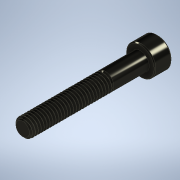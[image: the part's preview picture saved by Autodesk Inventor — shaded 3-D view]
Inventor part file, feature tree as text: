
AUTODESK INVENTOR PART (.ipt)
format: ipt  version: 2020 (Build 240168000, 168)  size: 840,704 bytes
history: native  units: in
note: dims shown in document units (in); Inventor stores cm internally (conversion verified against a paired STEP export)
features: chamfer x1
ambient origin geometry x8: Origin, YZ Plane, XZ Plane, XY Plane, X Axis, Y Axis, Z Axis, Center Point
bodies: Solid1 (feature_tree)
feature tree (1):
  chamfer  "Chamfer2"  [1 undecoded]
note: 1 required parameter value undecoded (feature->parameter linkage not recoverable at this tier; creation-order binding heuristic only, values carry confidence <= 0.55)
